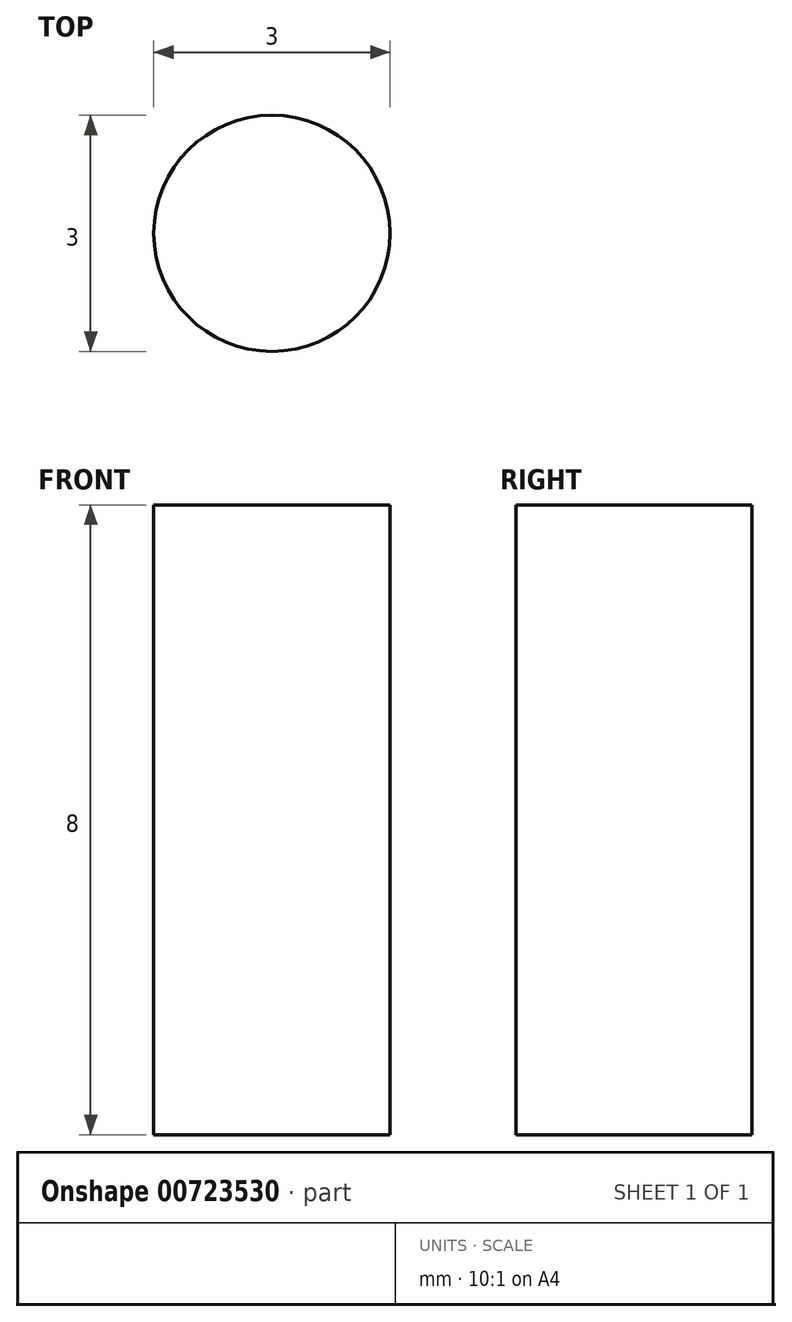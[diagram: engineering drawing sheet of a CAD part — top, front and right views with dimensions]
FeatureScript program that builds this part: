
annotation { "Feature Type Name" : "Feature", "Feature Type Description" : "" }
export const myFeature = defineFeature(function(context is Context, id is Id, definition is map)
    precondition{}
    {
        {
            var Q0;
            Q0=qCreatedBy(makeId("Top.planeOp"),FACE);
            var sketch = newSketch(context, id + "F0", { "sketchPlane" : qUnion([Q0])});
            skCircle(sketch, "E0", {"center": v(0, 0) * mm, "radius": 1.5 * mm});
            skSolve(sketch);
        }
        {
            var Q0;
            Q0 = qSketchRegion(id + "F0", true);
            extrude(context, id + "F1", {"entities" : qUnion([Q0]), "depth" : 8 * mm, "offsetDistance" : 25 * mm});
        }
    });
